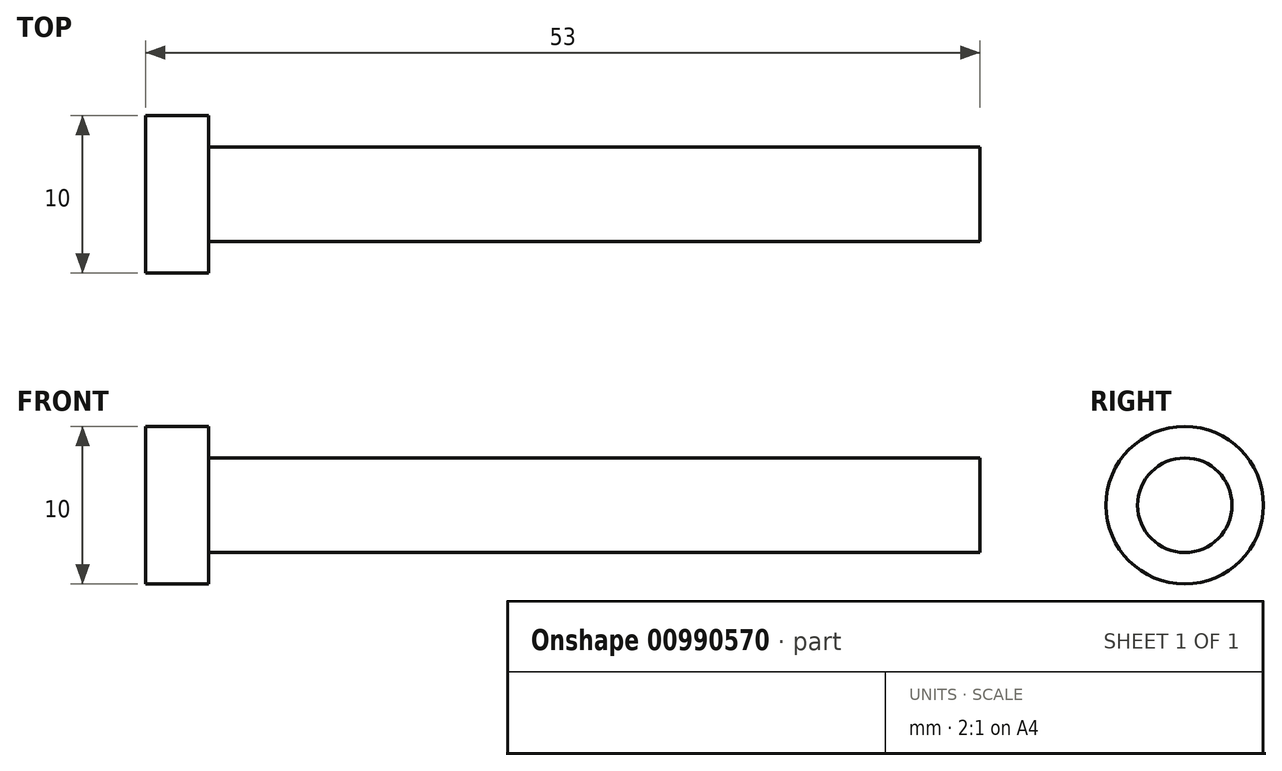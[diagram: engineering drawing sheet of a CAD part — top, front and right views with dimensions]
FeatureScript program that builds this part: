
annotation { "Feature Type Name" : "Feature", "Feature Type Description" : "" }
export const myFeature = defineFeature(function(context is Context, id is Id, definition is map)
    precondition{}
    {
        {
            var Q0;
            Q0=qCreatedBy(makeId("Right.planeOp"),FACE);
            var sketch = newSketch(context, id + "F0", { "sketchPlane" : qUnion([Q0])});
            skCircle(sketch, "E0", {"center": v(0, 0) * mm, "radius": 3 * mm});
            skCircle(sketch, "E1", {"center": v(0, 0) * mm, "radius": 5 * mm});
            skSolve(sketch);
        }
        {
            var Q0;
            Q0=makeQuery(id+"F0.imprint","IMPRINT",FACE,{"disambiguationData":[TD([[makeQuery(id+"F0.imprint","IMPRINT",EDGE,{"derivedFrom":sQuery(id+"F0.wireOp",EDGE,"E0")}),1.0]])]});
            extrude(context, id + "F1", {"entities" : qUnion([Q0]), "depth" : 49 * mm, "offsetDistance" : 25.4 * mm});
        }
        {
            var Q0;
            Q0=makeQuery(id+"F0.imprint","IMPRINT",FACE,{"disambiguationData":[TD([[makeQuery(id+"F0.imprint","IMPRINT",EDGE,{"derivedFrom":sQuery(id+"F0.wireOp",EDGE,"E0")}),-1.0]])]});
            var Q1;
            Q1=makeQuery(id+"F0.imprint","IMPRINT",FACE,{"disambiguationData":[TD([[makeQuery(id+"F0.imprint","IMPRINT",EDGE,{"derivedFrom":sQuery(id+"F0.wireOp",EDGE,"E0")}),1.0]])]});
            extrude(context, id + "F2", {"entities" : qUnion([Q0, Q1]), "operationType" : NewBodyOperationType.ADD, "oppositeDirection" : true, "depth" : 4 * mm, "offsetDistance" : 25.4 * mm});
        }
    });
